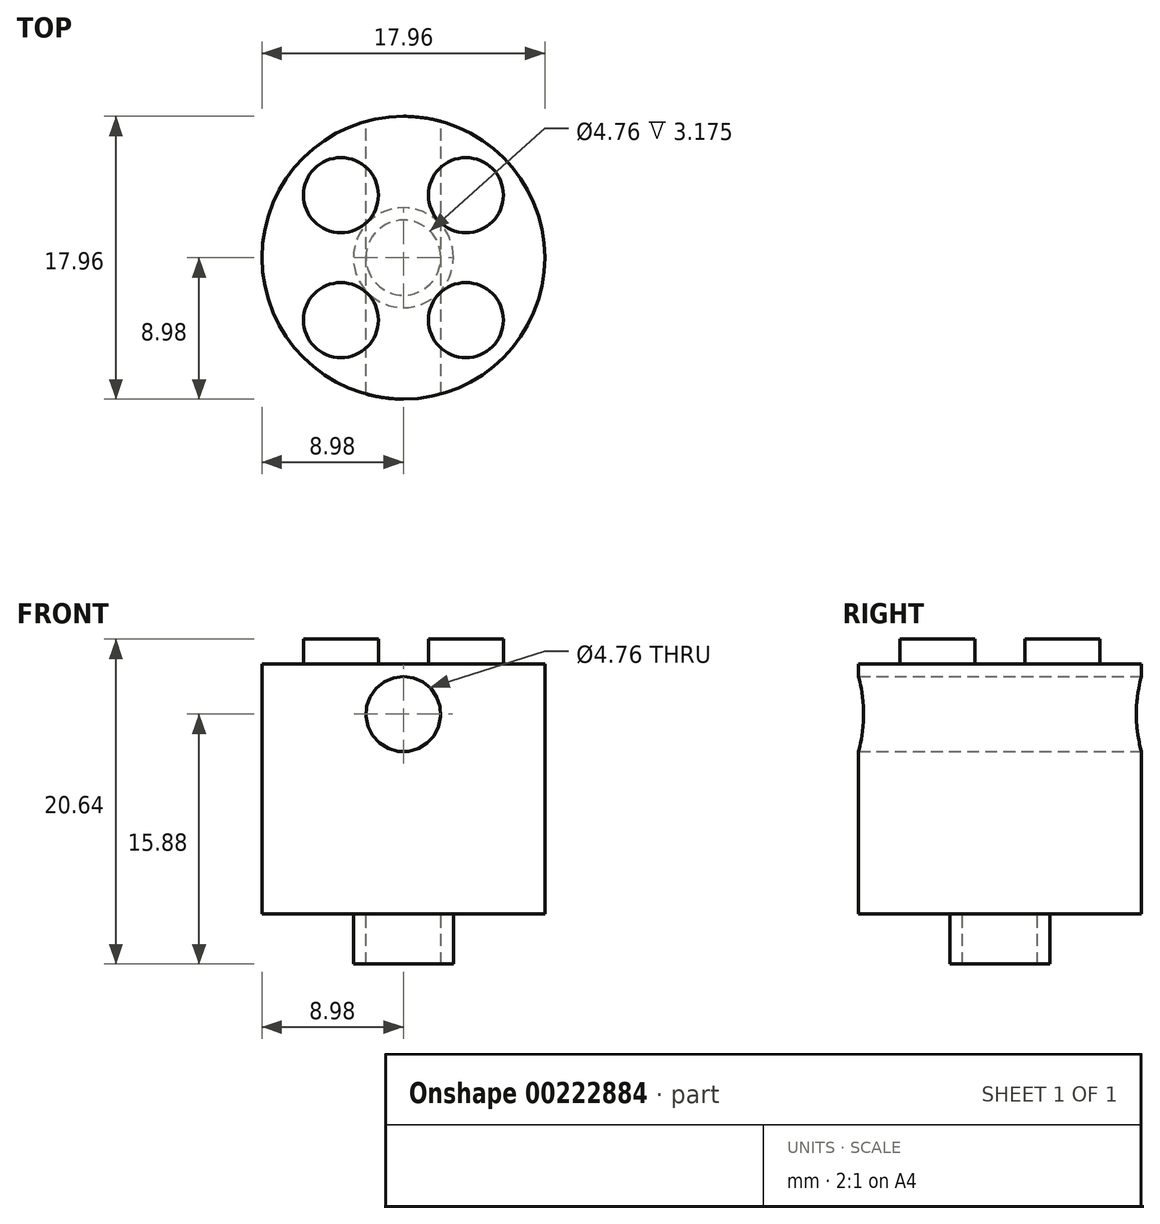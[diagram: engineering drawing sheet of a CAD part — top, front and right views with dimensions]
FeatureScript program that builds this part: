
annotation { "Feature Type Name" : "Feature", "Feature Type Description" : "" }
export const myFeature = defineFeature(function(context is Context, id is Id, definition is map)
    precondition{}
    {
        {
            var Q0;
            Q0=qCreatedBy(makeId("Top.planeOp"),FACE);
            var sketch = newSketch(context, id + "F0", { "sketchPlane" : qUnion([Q0])});
            skPoint(sketch, "E0.middle", {"position": v(0, 0) * mm});
            skCircle(sketch, "E1", {"center": v(0, 0) * mm, "radius": 8.98 * mm});
            skSolve(sketch);
        }
        {
            var Q0;
            Q0=makeQuery(id+"F0.imprint","IMPRINT",FACE,{"disambiguationData":[TD([[makeQuery(id+"F0.imprint","IMPRINT",EDGE,{"derivedFrom":sQuery(id+"F0.wireOp",EDGE,"E1")}),1.0]])]});
            extrude(context, id + "F1", {"entities" : qUnion([Q0]), "depth" : 15.88 * mm});
        }
        {
            var Q0;
            Q0=makeQuery(id+"F1.opExtrude","CAP_FACE",FACE,{"disambiguationData":[OSD([sQuery(id+"F0.wireOp",EDGE,"E1")])],"isStart":true});
            var sketch = newSketch(context, id + "F2", { "sketchPlane" : qUnion([Q0])});
            skCircle(sketch, "E2", {"center": v(0, 0) * mm, "radius": 3.18 * mm});
            skCircle(sketch, "E3.0", {"center": v(0, 0) * mm, "radius": 2.38 * mm});
            skSolve(sketch);
        }
        {
            var Q0;
            Q0 = qSketchRegion(id + "F2", true);
            extrude(context, id + "F3", {"entities" : qUnion([Q0]), "operationType" : NewBodyOperationType.ADD, "depth" : 3.17 * mm});
        }
        {
            var Q0;
            Q0=makeQuery(id+"F1.opExtrude","CAP_FACE",FACE,{"disambiguationData":[OSD([sQuery(id+"F0.wireOp",EDGE,"E1")])],"isStart":false});
            var sketch = newSketch(context, id + "F4", { "sketchPlane" : qUnion([Q0])});
            skLineSegment(sketch, "E4", {"start": v(0, 0) * mm, "end": v(0, 8.98) * mm});
            skLineSegment(sketch, "E5", {"start": v(0, 0) * mm, "end": v(0, -8.98) * mm});
            skLineSegment(sketch, "E6", {"start": v(0, 0) * mm, "end": v(8.98, 0) * mm});
            skLineSegment(sketch, "E7", {"start": v(0, 0) * mm, "end": v(-8.98, 0) * mm});
            skPoint(sketch, "E8", {"position": v(-3.97, 0) * mm});
            skPoint(sketch, "E9", {"position": v(0, -3.97) * mm});
            skPoint(sketch, "E10.MirrorP", {"position": v(3.97, 0) * mm});
            skPoint(sketch, "E11.MirrorP", {"position": v(0, 3.97) * mm});
            skCircle(sketch, "E12", {"center": v(-3.97, 3.97) * mm, "radius": 2.38 * mm});
            skCircle(sketch, "E13", {"center": v(3.97, 3.97) * mm, "radius": 2.38 * mm});
            skCircle(sketch, "E14.MirrorC", {"center": v(3.97, -3.97) * mm, "radius": 2.38 * mm});
            skCircle(sketch, "E15.MirrorC", {"center": v(-3.97, -3.97) * mm, "radius": 2.38 * mm});
            skSolve(sketch);
        }
        {
            var Q0;
            Q0 = qSketchRegion(id + "F4", true);
            extrude(context, id + "F5", {"entities" : qUnion([Q0]), "operationType" : NewBodyOperationType.ADD, "depth" : 1.59 * mm});
        }
        {
            var Q0;
            Q0=qCreatedBy(makeId("Front.planeOp"),FACE);
            var sketch = newSketch(context, id + "F6", { "sketchPlane" : qUnion([Q0])});
            skLineSegment(sketch, "E16", {"start": v(0, 0) * mm, "end": v(0, 12.7) * mm});
            skCircle(sketch, "E17", {"center": v(0, 12.7) * mm, "radius": 2.38 * mm});
            skSolve(sketch);
        }
        {
            var Q0;
            Q0 = qSketchRegion(id + "F6", true);
            extrude(context, id + "F7", {"entities" : qUnion([Q0]), "operationType" : NewBodyOperationType.REMOVE, "endBound" : BoundingType.SYMMETRIC, "depth" : 25.4 * mm});
        }
    });
